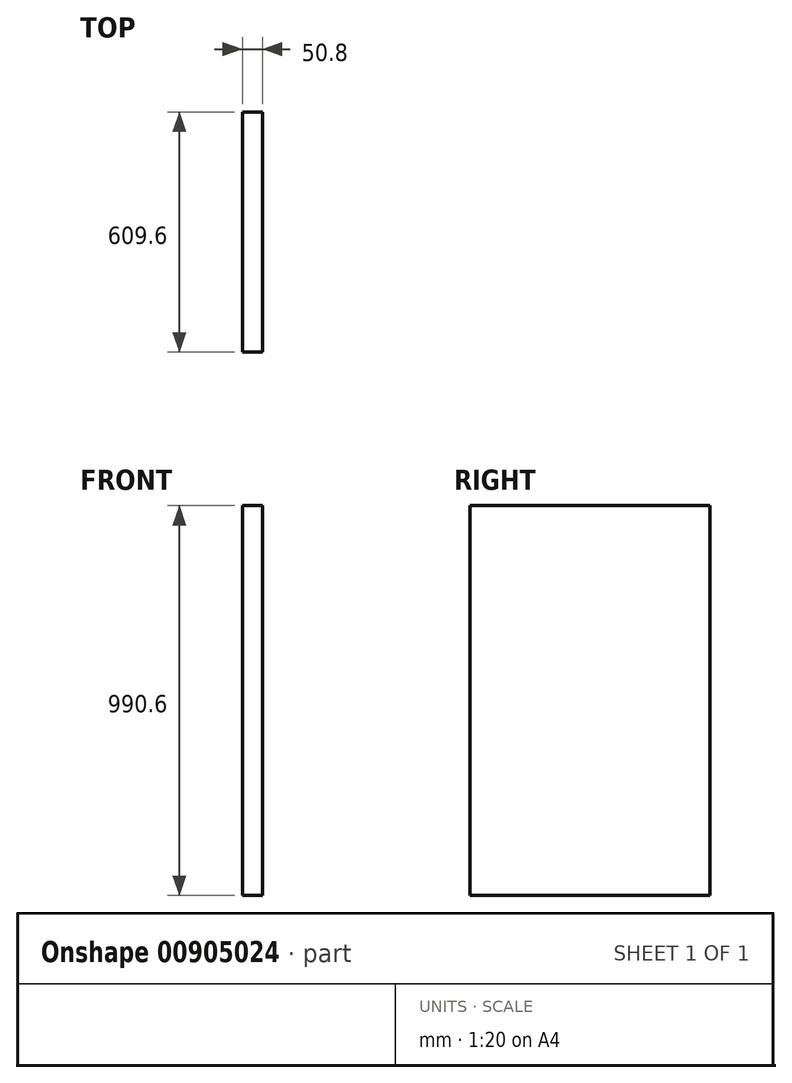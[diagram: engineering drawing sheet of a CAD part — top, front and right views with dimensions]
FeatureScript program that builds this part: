
annotation { "Feature Type Name" : "Feature", "Feature Type Description" : "" }
export const myFeature = defineFeature(function(context is Context, id is Id, definition is map)
    precondition{}
    {
        {
            var Q0;
            Q0=qCreatedBy(makeId("Front.planeOp"),FACE);
            var sketch = newSketch(context, id + "F0", { "sketchPlane" : qUnion([Q0])});
            skLineSegment(sketch, "E0.bottom", {"start": v(-86.42, 481.44) * mm, "end": v(-35.62, 481.44) * mm});
            skLineSegment(sketch, "E0.top", {"start": v(-86.42, -509.16) * mm, "end": v(-35.62, -509.16) * mm});
            skLineSegment(sketch, "E0.left", {"start": v(-86.42, 481.44) * mm, "end": v(-86.42, -509.16) * mm});
            skLineSegment(sketch, "E0.right", {"start": v(-35.62, 481.44) * mm, "end": v(-35.62, -509.16) * mm});
            skSolve(sketch);
        }
        {
            var Q0;
            Q0=makeQuery(id+"F0.imprint","IMPRINT",FACE,{"disambiguationData":[TD([[makeQuery(id+"F0.imprint","IMPRINT",EDGE,{"derivedFrom":sQuery(id+"F0.wireOp",EDGE,"E0.bottom")}),-1.0]])]});
            extrude(context, id + "F1", {"entities" : qUnion([Q0]), "depth" : 609.6 * mm, "offsetDistance" : 25.4 * mm});
        }
    });
